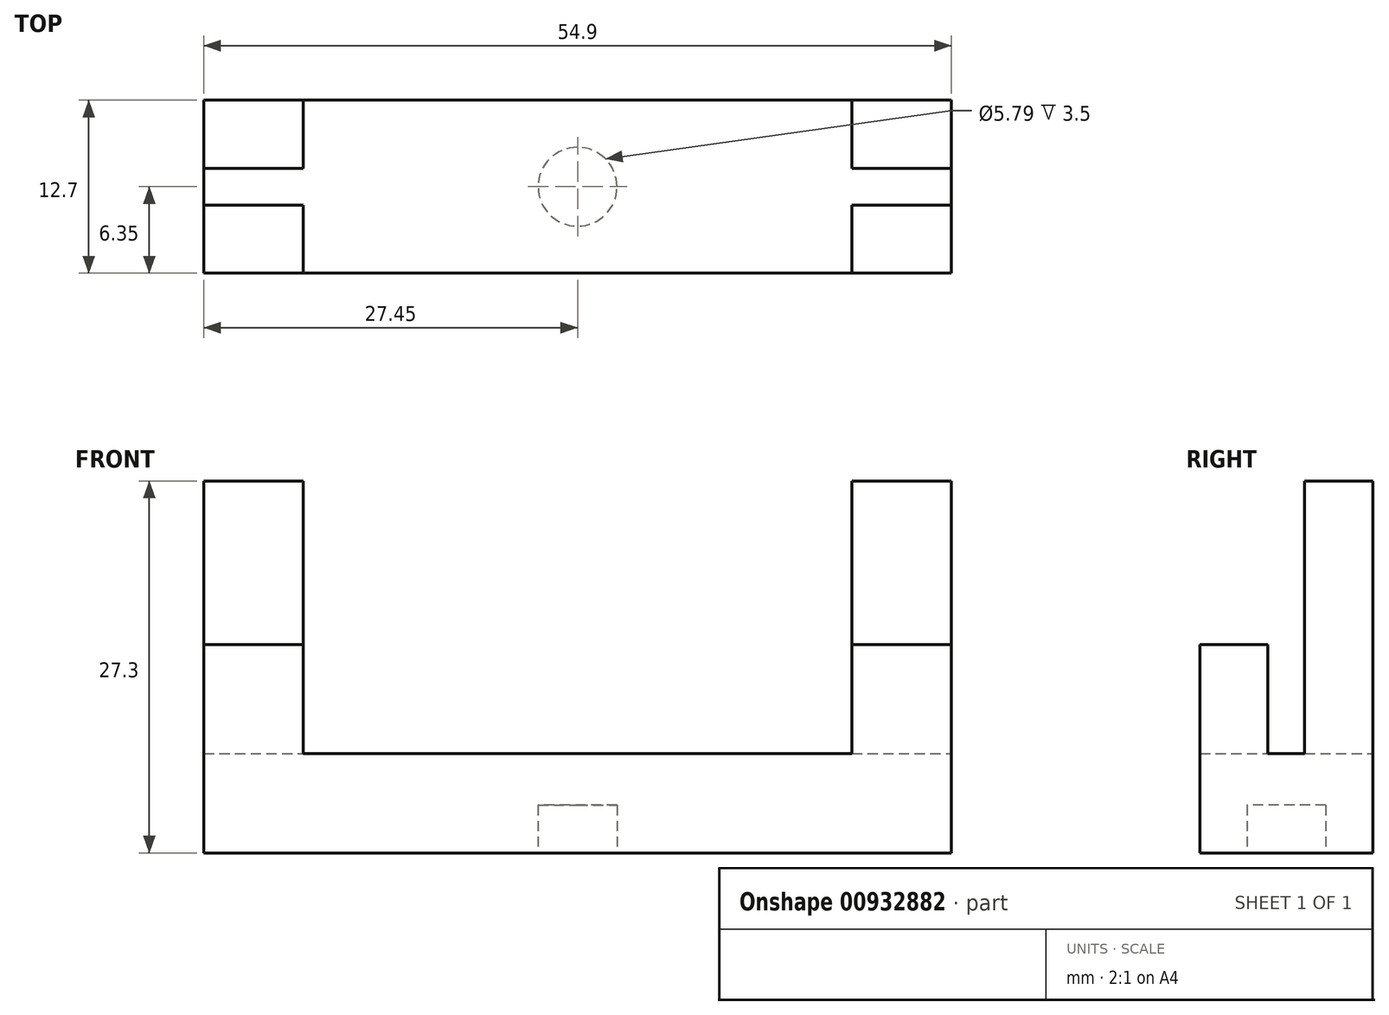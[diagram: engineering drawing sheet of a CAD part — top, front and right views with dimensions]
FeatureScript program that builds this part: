
annotation { "Feature Type Name" : "Feature", "Feature Type Description" : "" }
export const myFeature = defineFeature(function(context is Context, id is Id, definition is map)
    precondition{}
    {
        {
            var Q0;
            Q0=qCreatedBy(makeId("Top.planeOp"),FACE);
            var sketch = newSketch(context, id + "F0", { "sketchPlane" : qUnion([Q0])});
            skLineSegment(sketch, "E0", {"start": v(20.15, 0) * mm, "end": v(20.15, 10) * mm});
            skLineSegment(sketch, "E1", {"start": v(-20.15, 0) * mm, "end": v(-20.15, 10) * mm});
            skLineSegment(sketch, "E2", {"start": v(-20.15, 0) * mm, "end": v(-20.15, -10) * mm});
            skLineSegment(sketch, "E3", {"start": v(20.15, 0) * mm, "end": v(20.15, -10) * mm});
            skLineSegment(sketch, "E4", {"start": v(-20.15, -10) * mm, "end": v(20.15, -10) * mm});
            skLineSegment(sketch, "E5", {"start": v(-20.15, 10) * mm, "end": v(-27.45, 10) * mm});
            skLineSegment(sketch, "E6", {"start": v(-27.45, 10) * mm, "end": v(-27.45, -10) * mm});
            skLineSegment(sketch, "E7", {"start": v(-27.45, -10) * mm, "end": v(-27.45, -17.3) * mm});
            skLineSegment(sketch, "E8", {"start": v(20.15, 10) * mm, "end": v(27.45, 10) * mm});
            skLineSegment(sketch, "E9", {"start": v(27.45, 10) * mm, "end": v(27.45, -10) * mm});
            skLineSegment(sketch, "E10", {"start": v(27.45, -10) * mm, "end": v(27.45, -17.3) * mm});
            skLineSegment(sketch, "E11", {"start": v(27.45, -17.3) * mm, "end": v(-27.45, -17.3) * mm});
            skSolve(sketch);
        }
        {
            var Q0;
            Q0 = qSketchRegion(id + "F0", true);
            extrude(context, id + "F1", {"entities" : qUnion([Q0]), "depth" : 12.7 * mm, "offsetDistance" : 25 * mm});
        }
        {
            var Q0;
            Q0=makeQuery(id+"F1.opExtrude","SWEPT_BODY",BODY,{"disambiguationData":[OSD([sQuery(id+"F0.wireOp",EDGE,"E0"),sQuery(id+"F0.wireOp",EDGE,"E1"),sQuery(id+"F0.wireOp",EDGE,"E2"),sQuery(id+"F0.wireOp",EDGE,"E3"),sQuery(id+"F0.wireOp",EDGE,"E4"),sQuery(id+"F0.wireOp",EDGE,"E5"),sQuery(id+"F0.wireOp",EDGE,"E6"),sQuery(id+"F0.wireOp",EDGE,"E7"),sQuery(id+"F0.wireOp",EDGE,"E8"),sQuery(id+"F0.wireOp",EDGE,"E9"),sQuery(id+"F0.wireOp",EDGE,"E10"),sQuery(id+"F0.wireOp",EDGE,"E11")])]});
            var Q1;
            Q1=makeQuery(id+"F1.opExtrude","CAP_EDGE",EDGE,{"disambiguationData":[OSD([sQuery(id+"F0.wireOp",EDGE,"E11")])],"isStart":false});
            transform(context, id + "F2", {"entities" : qUnion([Q0]), "transformType" : TransformType.ROTATION, "transformAxis" : qUnion([Q1]), "angle" : 270 * degree, "makeCopy" : false});
        }
        {
            var Q0;
            Q0=makeQuery(id+"F1.opExtrude","CAP_FACE",FACE,{"disambiguationData":[OSD([sQuery(id+"F0.wireOp",EDGE,"E0"),sQuery(id+"F0.wireOp",EDGE,"E1"),sQuery(id+"F0.wireOp",EDGE,"E2"),sQuery(id+"F0.wireOp",EDGE,"E3"),sQuery(id+"F0.wireOp",EDGE,"E4"),sQuery(id+"F0.wireOp",EDGE,"E5"),sQuery(id+"F0.wireOp",EDGE,"E6"),sQuery(id+"F0.wireOp",EDGE,"E7"),sQuery(id+"F0.wireOp",EDGE,"E8"),sQuery(id+"F0.wireOp",EDGE,"E9"),sQuery(id+"F0.wireOp",EDGE,"E10"),sQuery(id+"F0.wireOp",EDGE,"E11")])],"isStart":false});
            var sketch = newSketch(context, id + "F3", { "sketchPlane" : qUnion([Q0])});
            skLineSegment(sketch, "E12", {"start": v(20.15, 28) * mm, "end": v(27.45, 28) * mm});
            skLineSegment(sketch, "E13", {"start": v(27.45, 40) * mm, "end": v(20.15, 40) * mm});
            skLineSegment(sketch, "E14", {"start": v(20.15, 40) * mm, "end": v(20.15, 28) * mm});
            skLineSegment(sketch, "E15", {"start": v(27.45, 28) * mm, "end": v(27.45, 40) * mm});
            skLineSegment(sketch, "E16", {"start": v(-20.15, 28) * mm, "end": v(-27.45, 28) * mm});
            skLineSegment(sketch, "E17", {"start": v(-27.45, 28) * mm, "end": v(-27.45, 40) * mm});
            skLineSegment(sketch, "E18", {"start": v(-27.45, 40) * mm, "end": v(-20.15, 40) * mm});
            skLineSegment(sketch, "E19", {"start": v(-20.15, 40) * mm, "end": v(-20.15, 28) * mm});
            skSolve(sketch);
        }
        {
            var Q0;
            Q0 = qSketchRegion(id + "F3", true);
            extrude(context, id + "F4", {"entities" : qUnion([Q0]), "operationType" : NewBodyOperationType.REMOVE, "oppositeDirection" : true, "depth" : 7.2 * mm, "offsetDistance" : 25 * mm});
        }
        {
            var Q0;
            Q0=makeQuery(id+"F1.opExtrude","SWEPT_FACE",FACE,{"disambiguationData":[OSD([sQuery(id+"F0.wireOp",EDGE,"E9"),sQuery(id+"F0.wireOp",EDGE,"E10")])]});
            var sketch = newSketch(context, id + "F5", { "sketchPlane" : qUnion([Q0])});
            skLineSegment(sketch, "E20", {"start": v(-12.3, 28) * mm, "end": v(-12.3, 20) * mm});
            skLineSegment(sketch, "E21", {"start": v(-12.3, 20) * mm, "end": v(-9.6, 20) * mm});
            skLineSegment(sketch, "E22", {"start": v(-9.6, 20) * mm, "end": v(-9.6, 40) * mm});
            skLineSegment(sketch, "E23.bottom", {"start": v(-9.6, 20) * mm, "end": v(-9.6, 20) * mm});
            skLineSegment(sketch, "E23.top", {"start": v(-9.6, 40) * mm, "end": v(-9.6, 40) * mm});
            skLineSegment(sketch, "E24.top", {"start": v(-12.3, 40) * mm, "end": v(-9.6, 40) * mm});
            skLineSegment(sketch, "E24.left", {"start": v(-12.3, 20) * mm, "end": v(-12.3, 40) * mm});
            skSolve(sketch);
        }
        {
            var Q0;
            Q0 = qSketchRegion(id + "F5", true);
            extrude(context, id + "F6", {"entities" : qUnion([Q0]), "operationType" : NewBodyOperationType.REMOVE, "oppositeDirection" : true, "depth" : 54.9 * mm, "offsetDistance" : 25 * mm});
        }
        {
            var Q0;
            Q0=makeQuery(id+"F1.opExtrude","SWEPT_FACE",FACE,{"disambiguationData":[OSD([sQuery(id+"F0.wireOp",EDGE,"E11")])]});
            var sketch = newSketch(context, id + "F7", { "sketchPlane" : qUnion([Q0])});
            skPoint(sketch, "E25.endSnap0", {"position": v(-27.45, 10.95) * mm});
            skCircle(sketch, "E26", {"center": v(0, 10.95) * mm, "radius": 2.9 * mm});
            skSolve(sketch);
        }
        {
            var Q0;
            Q0 = qSketchRegion(id + "F7", true);
            extrude(context, id + "F8", {"entities" : qUnion([Q0]), "operationType" : NewBodyOperationType.REMOVE, "oppositeDirection" : true, "depth" : 3.5 * mm, "offsetDistance" : 25 * mm});
        }
        {
            var Q0;
            Q0=makeQuery(id+"F1.opExtrude","SWEPT_BODY",BODY,{"disambiguationData":[OSD([sQuery(id+"F0.wireOp",EDGE,"E0"),sQuery(id+"F0.wireOp",EDGE,"E1"),sQuery(id+"F0.wireOp",EDGE,"E2"),sQuery(id+"F0.wireOp",EDGE,"E3"),sQuery(id+"F0.wireOp",EDGE,"E4"),sQuery(id+"F0.wireOp",EDGE,"E5"),sQuery(id+"F0.wireOp",EDGE,"E6"),sQuery(id+"F0.wireOp",EDGE,"E7"),sQuery(id+"F0.wireOp",EDGE,"E8"),sQuery(id+"F0.wireOp",EDGE,"E9"),sQuery(id+"F0.wireOp",EDGE,"E10"),sQuery(id+"F0.wireOp",EDGE,"E11")])]});
            transform(context, id + "F9", {"entities" : qUnion([Q0]), "transformType" : TransformType.TRANSLATION_3D, "dx" : 0 * mm, "dy" : 10.95 * mm, "dz" : -12.7 * mm, "makeCopy" : false});
        }
    });
